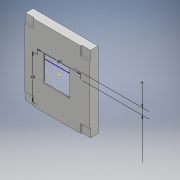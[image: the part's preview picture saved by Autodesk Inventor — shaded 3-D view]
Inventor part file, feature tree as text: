
AUTODESK INVENTOR PART (.ipt)
format: ipt  version: 2018 (Build 220112000, 112)  size: 167,936 bytes
history: native  units: mm
features: sketch x8, extrude x5
ambient origin geometry x8: Origin, YZ Plane, XZ Plane, XY Plane, X Axis, Y Axis, Z Axis, Center Point
bodies: Solid1 (feature_tree)
feature tree (13):
  extrude  "Extrusion1"  Depth=70.0mm
  extrude  "Extrusion2"  Depth=64.0mm
  extrude  "Extrusion3"  Depth=6.0mm TaperAngle=0.0deg
  extrude  "Extrusion4"  Depth=24.0mm
  sketch  "Sketch5"  dims[d10=26.0mm d11=26.0mm]
  sketch  "Sketch6"  dims[d16=1.5mm d17=0.0mm]
  sketch  "Sketch7"  dims[d18=24.0mm]
  extrude  "Extrusion5"  Depth=26.0mm
  sketch  "Sketch1"  dims[d0=60.0mm d1=70.0mm]
  sketch  "Sketch2"  dims[d2=8.0mm d3=0.0mm d4=64.0mm]
  sketch  "Sketch3"  dims[d5=54.0mm d6=6.0mm d7=0.0mm]
  sketch  "Sketch4"  dims[d8=24.0mm d9=24.0mm]
  sketch  "Sketch8"  dims[d19=24.0mm d20=1.5mm d21=0.0mm d23=3.0mm d24=3.0mm d25=3.0mm d26=3.0mm d27=40.0mm d28=40.0mm d29=6.0mm d30=8.0mm d31=8.0mm d32=8.0mm d33=8.0mm d34=8.0mm d35=8.0mm d36=8.0mm d37=8.0mm d38=1.0mm d39=0.0mm]
